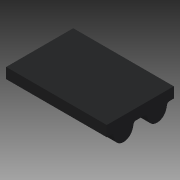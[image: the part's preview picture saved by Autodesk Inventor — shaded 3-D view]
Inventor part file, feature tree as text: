
AUTODESK INVENTOR PART (.ipt)
format: ipt  version: 2015 (Build 190159000, 159)  size: 109,568 bytes
history: native  units: in
note: dims shown in document units (in); Inventor stores cm internally (conversion verified against a paired STEP export)
features: other x5, plane x2, imported_body x1
ambient origin geometry x8: Origin, YZ Plane, XZ Plane, XY Plane, X Axis, Y Axis, Z Axis, Center Point
bodies: Body1 (feature_tree)
feature tree (8):
  other  "Бобышка-Вытянуть1"
  other  "GT2_cut1"
  plane  "Work Plane1"
  other  "Work Axis1"
  other  "Work Axis2"
  other  "Work Axis3"
  imported_body  "Base1"
  plane  "Work Plane2"
